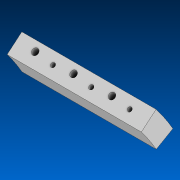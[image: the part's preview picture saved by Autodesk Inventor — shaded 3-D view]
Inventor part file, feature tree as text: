
AUTODESK INVENTOR PART (.ipt)
format: ipt  version: 2022 (Build 260153000, 153)  size: 139,776 bytes
history: native  units: in
note: dims shown in document units (in); Inventor stores cm internally (conversion verified against a paired STEP export)
features: sketch x5, extrude x2, hole x2, pattern_linear x2, plane x1
ambient origin geometry x8: Origin, YZ Plane, XZ Plane, XY Plane, X Axis, Y Axis, Z Axis, Center Point
bodies: Solid1 (feature_tree)
feature tree (12):
  extrude  "Extrusion1"  Depth=10.9074in
  hole  "Hole2"  [1 undecoded]
  pattern_linear  "Rectangular Pattern2"  Count1=3 Spacing1=2.0in
  sketch  "Sketch5"  dims[d6=7.0in d7=0.0in]
  hole  "Hole3"  [1 undecoded]
  plane  "Work Plane1"
  extrude  "Extrusion2"  Depth=1.0in
  pattern_linear  "Rectangular Pattern3"  Spacing1=1.0in  [1 undecoded]
  sketch  "Sketch1"  dims[d1=10.9074in d2=0.2749in]
  sketch  "Sketch3"  dims[d4=1.0in d5=1.0in]
  sketch  "Sketch6"  dims[d17=1.0in]
  sketch  "Sketch7"  dims[d18=0.5in d19=0.175in d20=0.75in d21=0.22in d22=0.325in d23=0.5635in d24=1.5in d25=0.0in d29=1.1811in d31=2.0in d32=30.0deg d33=1.0in d34=1.0in d35=0.5115in d36=0.175in d37=0.75in d38=0.22in d39=0.325in d40=0.5635in d41=1.5in d42=0.0in d43=-1.0in d44=0.32in d45=0.0in d46=0.0in d47=1.1811in d49=2.0in]
note: 3 required parameter values undecoded (feature->parameter linkage not recoverable at this tier; creation-order binding heuristic only, values carry confidence <= 0.55)
